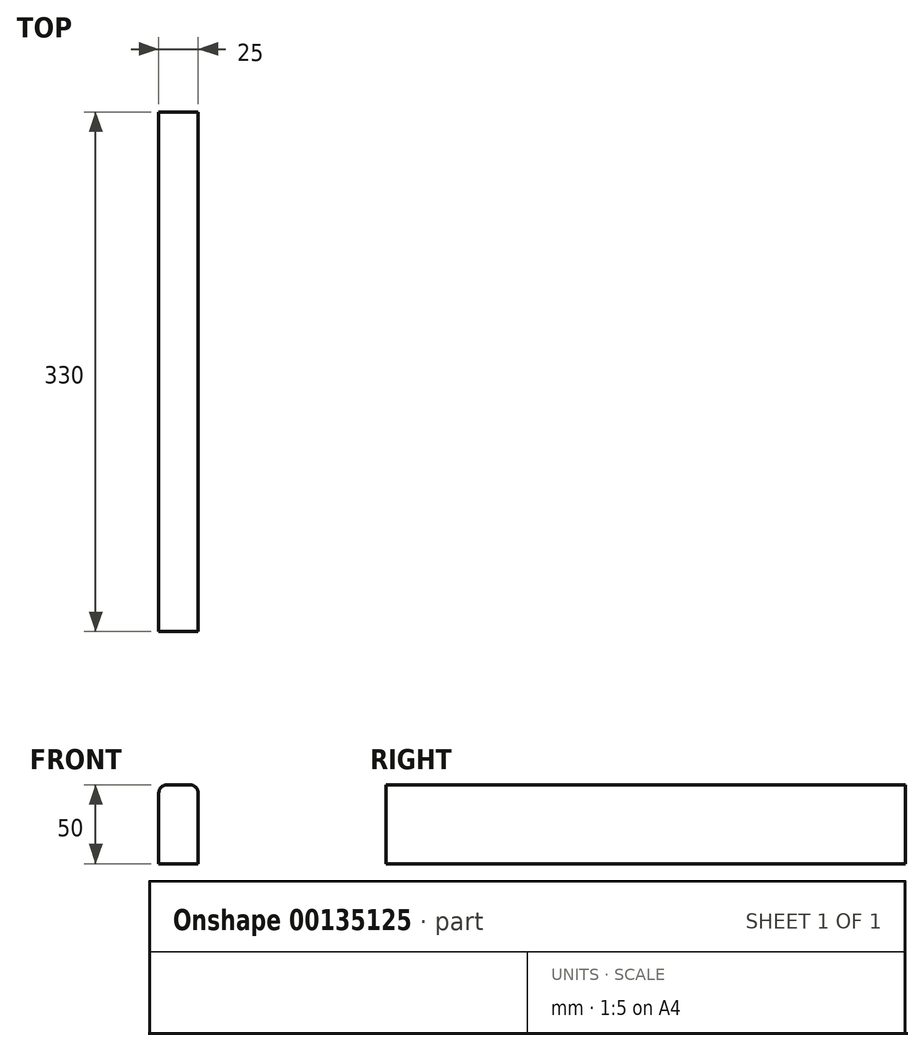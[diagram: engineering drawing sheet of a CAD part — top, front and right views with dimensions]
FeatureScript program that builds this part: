
annotation { "Feature Type Name" : "Feature", "Feature Type Description" : "" }
export const myFeature = defineFeature(function(context is Context, id is Id, definition is map)
    precondition{}
    {
        {
            var Q0;
            Q0=qCreatedBy(makeId("Front.planeOp"),FACE);
            var sketch = newSketch(context, id + "F0", { "sketchPlane" : qUnion([Q0])});
            skLineSegment(sketch, "E0.bottom", {"start": v(0, 0) * mm, "end": v(25, 0) * mm});
            skLineSegment(sketch, "E0.top", {"start": v(5, 50) * mm, "end": v(20, 50) * mm});
            skLineSegment(sketch, "E0.left", {"start": v(0, 0) * mm, "end": v(0, 45) * mm});
            skLineSegment(sketch, "E0.right", {"start": v(25, 0) * mm, "end": v(25, 45) * mm});
            skPoint(sketch, "E1.visualSharp", {"position": v(0, 50) * mm});
            skArc(sketch, "E1.filletArc", {"start": v(5, 50) * mm, "mid": v(1.46, 48.54) * mm, "end": v(0, 45) * mm});
            skPoint(sketch, "E2.visualSharp", {"position": v(25, 50) * mm});
            skArc(sketch, "E2.filletArc", {"start": v(25, 45) * mm, "mid": v(23.54, 48.54) * mm, "end": v(20, 50) * mm});
            skSolve(sketch);
        }
        {
            var Q0;
            Q0=qSketchRegion(id+"F0",true);
            extrude(context, id + "F1", {"entities" : qUnion([Q0]), "depth" : 330 * mm});
        }
    });
